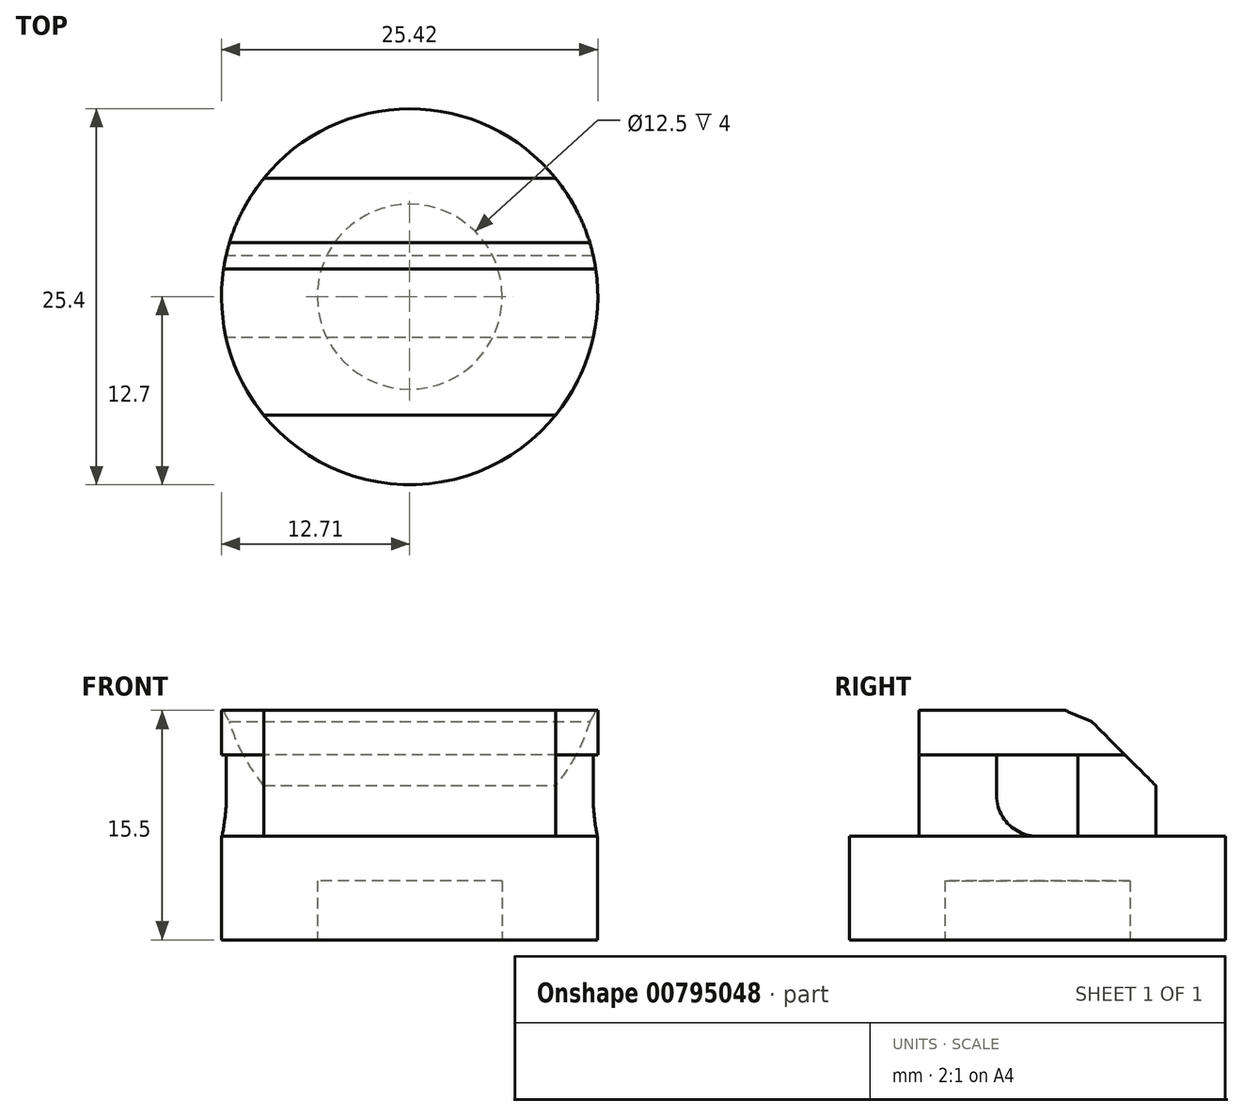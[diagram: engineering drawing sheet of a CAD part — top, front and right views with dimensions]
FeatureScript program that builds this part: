
annotation { "Feature Type Name" : "Feature", "Feature Type Description" : "" }
export const myFeature = defineFeature(function(context is Context, id is Id, definition is map)
    precondition{}
    {
        {
            var Q0;
            Q0=qCreatedBy(makeId("Top.planeOp"),FACE);
            var sketch = newSketch(context, id + "F0", { "sketchPlane" : qUnion([Q0])});
            skCircle(sketch, "E0", {"center": v(0, 0) * mm, "radius": 12.7 * mm});
            skCircle(sketch, "E1", {"center": v(0, 0) * mm, "radius": 6.25 * mm});
            skSolve(sketch);
        }
        {
            var Q0;
            Q0=makeQuery(id+"F0.imprint","IMPRINT",FACE,{"disambiguationData":[TD([[makeQuery(id+"F0.imprint","IMPRINT",EDGE,{"derivedFrom":sQuery(id+"F0.wireOp",EDGE,"E0")}),1.0]])]});
            extrude(context, id + "F1", {"entities" : qUnion([Q0]), "depth" : 4 * mm, "offsetDistance" : 25.4 * mm});
        }
        {
            var Q0;
            Q0=makeQuery(id+"F1.opExtrude","CAP_FACE",FACE,{"disambiguationData":[OSD([sQuery(id+"F0.wireOp",EDGE,"E0"),sQuery(id+"F0.wireOp",EDGE,"E1")])],"isStart":false});
            cPlane(context, id + "F2", {"entities" : qUnion([Q0]), "cplaneType" : CPlaneType.OFFSET, "offset" : 0 * mm, "width" : 152.4 * mm, "height" : 152.4 * mm});
        }
        {
            var Q0;
            Q0=qCreatedBy(id+"F2.planeOp",FACE);
            var sketch = newSketch(context, id + "F3", { "sketchPlane" : qUnion([Q0])});
            skCircle(sketch, "E2", {"center": v(0, 0) * mm, "radius": 12.7 * mm});
            skSolve(sketch);
        }
        {
            var Q0;
            Q0=makeQuery(id+"F3.imprint","IMPRINT",FACE,{"disambiguationData":[TD([[makeQuery(id+"F3.imprint","IMPRINT",EDGE,{"derivedFrom":sQuery(id+"F3.wireOp",EDGE,"E2")}),1.0]])]});
            extrude(context, id + "F4", {"entities" : qUnion([Q0]), "operationType" : NewBodyOperationType.ADD, "depth" : 3 * mm, "offsetDistance" : 25.4 * mm});
        }
        {
            var Q0;
            Q0=makeQuery(id+"F4.opExtrude","CAP_FACE",FACE,{"disambiguationData":[OSD([sQuery(id+"F3.wireOp",EDGE,"E2")])],"isStart":false});
            cPlane(context, id + "F5", {"entities" : qUnion([Q0]), "cplaneType" : CPlaneType.OFFSET, "offset" : 0 * mm, "width" : 152.4 * mm, "height" : 152.4 * mm});
        }
        {
            var Q0;
            Q0=qCreatedBy(id+"F5.planeOp",FACE);
            var sketch = newSketch(context, id + "F6", { "sketchPlane" : qUnion([Q0])});
            skLineSegment(sketch, "E3", {"start": v(30.9, 0) * mm, "end": v(30.9, 2.75) * mm, "construction": true});
            skLineSegment(sketch, "E4", {"start": v(29.5, 0) * mm, "end": v(29.5, 8) * mm, "construction": true});
            skLineSegment(sketch, "E5", {"start": v(12.39, 2.75) * mm, "end": v(-12.39, 2.75) * mm});
            skLineSegment(sketch, "E6", {"start": v(9.85, 8) * mm, "end": v(-9.85, 8) * mm});
            skArc(sketch, "E7", {"start": v(-9.85, 8) * mm, "mid": v(-11.43, 5.52) * mm, "end": v(-12.39, 2.75) * mm});
            skArc(sketch, "E8", {"start": v(12.39, 2.75) * mm, "mid": v(11.43, 5.52) * mm, "end": v(9.85, 8) * mm});
            skLineSegment(sketch, "E9.MirrorCS", {"start": v(12.39, -2.75) * mm, "end": v(-12.39, -2.75) * mm});
            skLineSegment(sketch, "E10.MirrorCS", {"start": v(9.85, -8) * mm, "end": v(-9.85, -8) * mm});
            skArc(sketch, "E11.MirrorCS", {"start": v(-9.85, -8) * mm, "mid": v(-11.43, -5.52) * mm, "end": v(-12.39, -2.75) * mm});
            skArc(sketch, "E12.MirrorCS", {"start": v(12.39, -2.75) * mm, "mid": v(11.43, -5.52) * mm, "end": v(9.85, -8) * mm});
            skLineSegment(sketch, "E13.bottom", {"start": v(0, 2.75) * mm, "end": v(-4.04, 2.75) * mm});
            skLineSegment(sketch, "E13.top", {"start": v(0, -2.75) * mm, "end": v(-4.04, -2.75) * mm});
            skLineSegment(sketch, "E13.left", {"start": v(0, 2.75) * mm, "end": v(0, -2.75) * mm});
            skLineSegment(sketch, "E13.right", {"start": v(-4.04, 2.75) * mm, "end": v(-4.04, -2.75) * mm});
            skLineSegment(sketch, "E14.bottom", {"start": v(30.9, 2.75) * mm, "end": v(-246457.58, 2.75) * mm});
            skLineSegment(sketch, "E14.top", {"start": v(30.9, -147527.56) * mm, "end": v(-246457.58, -147527.56) * mm});
            skLineSegment(sketch, "E14.left", {"start": v(30.9, 2.75) * mm, "end": v(30.9, -147527.56) * mm});
            skLineSegment(sketch, "E14.right", {"start": v(-246457.58, 2.75) * mm, "end": v(-246457.58, -147527.56) * mm});
            skLineSegment(sketch, "E15.bottom", {"start": v(30.9, 2.75) * mm, "end": v(-419819.12, 2.75) * mm});
            skLineSegment(sketch, "E15.top", {"start": v(30.9, -239114.76) * mm, "end": v(-419819.12, -239114.76) * mm});
            skLineSegment(sketch, "E15.left", {"start": v(30.9, 2.75) * mm, "end": v(30.9, -239114.76) * mm});
            skLineSegment(sketch, "E15.right", {"start": v(-419819.12, 2.75) * mm, "end": v(-419819.12, -239114.76) * mm});
            skLineSegment(sketch, "E16.bottom", {"start": v(30.9, 2.75) * mm, "end": v(-488509.55, 2.75) * mm});
            skLineSegment(sketch, "E16.top", {"start": v(30.9, -297992.25) * mm, "end": v(-488509.55, -297992.25) * mm});
            skLineSegment(sketch, "E16.left", {"start": v(30.9, 2.75) * mm, "end": v(30.9, -297992.25) * mm});
            skLineSegment(sketch, "E16.right", {"start": v(-488509.55, 2.75) * mm, "end": v(-488509.55, -297992.25) * mm});
            skLineSegment(sketch, "E17.bottom", {"start": v(30.9, 2.75) * mm, "end": v(-495402.83, 2.75) * mm});
            skLineSegment(sketch, "E17.top", {"start": v(30.9, -303457.61) * mm, "end": v(-495402.83, -303457.61) * mm});
            skLineSegment(sketch, "E17.left", {"start": v(30.9, 2.75) * mm, "end": v(30.9, -303457.61) * mm});
            skLineSegment(sketch, "E17.right", {"start": v(-495402.83, 2.75) * mm, "end": v(-495402.83, -303457.61) * mm});
            skSolve(sketch);
        }
        {
            var Q0;
            Q0=makeQuery(id+"F6.imprint","IMPRINT",FACE,{"disambiguationData":[TD([[makeQuery(id+"F6.imprint","IMPRINT",EDGE,{"derivedFrom":sQuery(id+"F6.wireOp",EDGE,"E5")}),-1.0]])]});
            var Q1;
            Q1=makeQuery(id+"F6.imprint","IMPRINT",FACE,{"disambiguationData":[TD([[makeQuery(id+"F6.imprint","IMPRINT",EDGE,{"derivedFrom":sQuery(id+"F6.wireOp",EDGE,"E9.MirrorCS")}),1.0]])]});
            var Q2;
            Q2=makeQuery(id+"F6.imprint","IMPRINT",FACE,{"disambiguationData":[TD([[makeQuery(id+"F6.imprint","IMPRINT",EDGE,{"derivedFrom":sQuery(id+"F6.wireOp",EDGE,"E6")}),1.0]])]});
            extrude(context, id + "F7", {"entities" : qUnion([Q0, Q1, Q2]), "operationType" : NewBodyOperationType.ADD, "depth" : 5.5 * mm, "offsetDistance" : 25.4 * mm});
        }
        {
            var Q0;
            Q0=makeQuery(id+"F7.opExtrude","CAP_FACE",FACE,{"disambiguationData":[OSD([sQuery(id+"F6.wireOp",EDGE,"E9.MirrorCS"),sQuery(id+"F6.wireOp",EDGE,"E10.MirrorCS"),sQuery(id+"F6.wireOp",EDGE,"E11.MirrorCS"),sQuery(id+"F6.wireOp",EDGE,"E12.MirrorCS"),sQuery(id+"F6.wireOp",EDGE,"E13.top")])],"isStart":false});
            cPlane(context, id + "F8", {"entities" : qUnion([Q0]), "cplaneType" : CPlaneType.OFFSET, "offset" : 0 * mm, "width" : 152.4 * mm, "height" : 152.4 * mm});
        }
        {
            var Q0;
            Q0=qCreatedBy(id+"F8.planeOp",FACE);
            var sketch = newSketch(context, id + "F9", { "sketchPlane" : qUnion([Q0])});
            skLineSegment(sketch, "E18", {"start": v(9.85, -8) * mm, "end": v(-9.85, -8) * mm});
            skArc(sketch, "E19", {"start": v(9.85, -8) * mm, "mid": v(12.68, 0) * mm, "end": v(9.85, 8) * mm});
            skArc(sketch, "E20.MirrorCS", {"start": v(-9.85, -8) * mm, "mid": v(-12.68, 0) * mm, "end": v(-9.85, 8) * mm});
            skLineSegment(sketch, "E21.MirrorCS", {"start": v(9.85, 8) * mm, "end": v(-9.85, 8) * mm});
            skArc(sketch, "E22", {"start": v(-9.85, 8) * mm, "mid": v(-12.71, 0) * mm, "end": v(-9.85, -8) * mm});
            skArc(sketch, "E23", {"start": v(9.85, -8) * mm, "mid": v(12.7, 0) * mm, "end": v(9.85, 8) * mm});
            skLineSegment(sketch, "E24", {"start": v(-9.85, -8) * mm, "end": v(9.85, -8) * mm});
            skSolve(sketch);
        }
        {
            var Q0;
            Q0 = qSketchRegion(id + "F9", true);
            extrude(context, id + "F10", {"entities" : qUnion([Q0]), "operationType" : NewBodyOperationType.ADD, "depth" : 3 * mm, "offsetDistance" : 25.4 * mm});
        }
        {
            var Q0;
            Q0=makeQuery(id+"F7.opExtrude","CAP_EDGE",EDGE,{"disambiguationData":[OSD([sQuery(id+"F6.wireOp",EDGE,"E9.MirrorCS"),sQuery(id+"F6.wireOp",EDGE,"E13.top")])],"isStart":true});
            var Q1;
            Q1=makeQuery(id+"F7.opExtrude","CAP_EDGE",EDGE,{"disambiguationData":[OSD([sQuery(id+"F6.wireOp",EDGE,"E9.MirrorCS"),sQuery(id+"F6.wireOp",EDGE,"E13.top")])],"isStart":false});
            var Q2;
            Q2=makeQuery(id+"F7.opExtrude","CAP_EDGE",EDGE,{"disambiguationData":[OSD([sQuery(id+"F6.wireOp",EDGE,"E17.bottom")])],"isStart":false});
            var Q3;
            Q3=makeQuery(id+"F7.opExtrude","CAP_EDGE",EDGE,{"disambiguationData":[OSD([sQuery(id+"F6.wireOp",EDGE,"E17.bottom")])],"isStart":true});
            fillet(context, id + "F11", {"entities" : qUnion([Q0, Q1, Q2, Q3]), "radius" : 2.75 * mm, "tangentPropagation" : true, "allowEdgeOverflow" : false});
        }
        {
            var Q0;
            Q0=makeQuery(id+"F10.opExtrude","CAP_EDGE",EDGE,{"disambiguationData":[OSD([sQuery(id+"F9.wireOp",EDGE,"E21.MirrorCS")])],"isStart":false});
            var Q1;
            Q1=makeQuery(id+"F10.opExtrude","CAP_EDGE",EDGE,{"disambiguationData":[OSD([sQuery(id+"F9.wireOp",EDGE,"E24")])],"isStart":false});
            chamfer(context, id + "F12", {"entities" : qUnion([Q0, Q1]), "width" : 5.08 * mm, "tangentPropagation" : true});
        }
        {
            var Q0;
            {var subQ0=sQuery(id+"F9.wireOp",EDGE,"E21.MirrorCS");Q0=makeQuery(id+"F12.opChamfer","BLEND_EDGE",EDGE,{"blendedFrom":[makeQuery(id+"F10.opExtrude","CAP_EDGE",EDGE,{"disambiguationData":[OSD([subQ0])],"isStart":false}),makeQuery(id+"F10.opExtrude","CAP_FACE",FACE,{"disambiguationData":[OSD([subQ0,sQuery(id+"F9.wireOp",EDGE,"E22"),sQuery(id+"F9.wireOp",EDGE,"E23"),sQuery(id+"F9.wireOp",EDGE,"E24")])],"isStart":false})],"blendedInto":[makeQuery(id+"F10.opExtrude","CAP_FACE",FACE,{"disambiguationData":[OSD([subQ0,sQuery(id+"F9.wireOp",EDGE,"E22"),sQuery(id+"F9.wireOp",EDGE,"E23"),sQuery(id+"F9.wireOp",EDGE,"E24")])],"isStart":false})]});}
            var Q1;
            {var subQ0=sQuery(id+"F9.wireOp",EDGE,"E24");Q1=makeQuery(id+"F12.opChamfer","BLEND_EDGE",EDGE,{"blendedFrom":[makeQuery(id+"F10.opExtrude","CAP_EDGE",EDGE,{"disambiguationData":[OSD([subQ0])],"isStart":false}),makeQuery(id+"F10.opExtrude","CAP_FACE",FACE,{"disambiguationData":[OSD([sQuery(id+"F9.wireOp",EDGE,"E21.MirrorCS"),sQuery(id+"F9.wireOp",EDGE,"E22"),sQuery(id+"F9.wireOp",EDGE,"E23"),subQ0])],"isStart":false})],"blendedInto":[makeQuery(id+"F10.opExtrude","CAP_FACE",FACE,{"disambiguationData":[OSD([sQuery(id+"F9.wireOp",EDGE,"E21.MirrorCS"),sQuery(id+"F9.wireOp",EDGE,"E22"),sQuery(id+"F9.wireOp",EDGE,"E23"),subQ0])],"isStart":false})]});}
            chamfer(context, id + "F13", {"entities" : qUnion([Q0, Q1]), "width" : 2.54 * mm, "tangentPropagation" : true});
        }
    });
